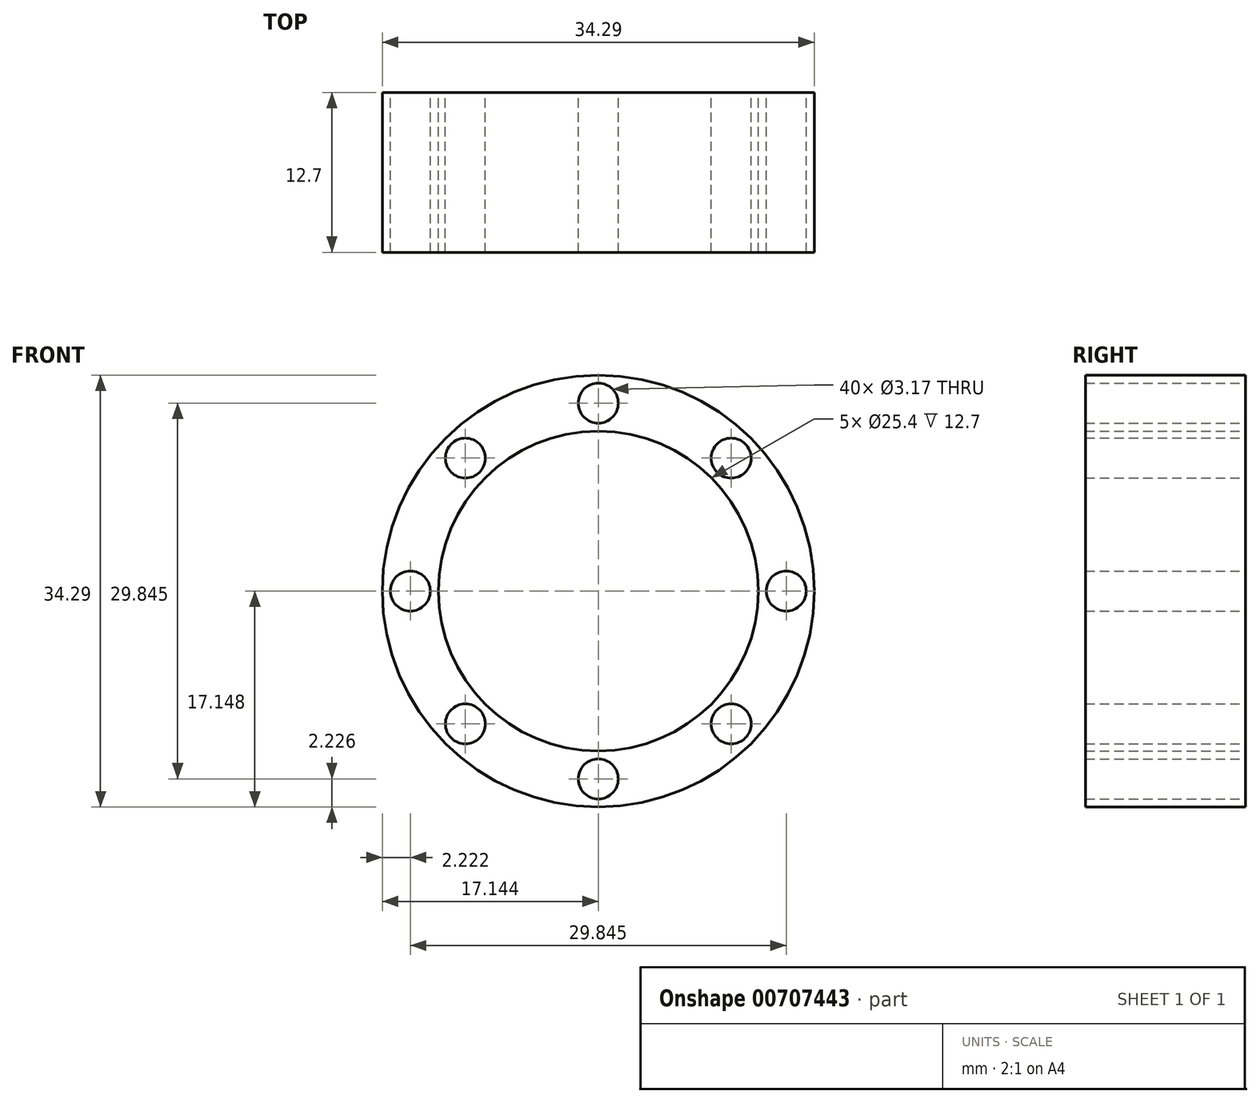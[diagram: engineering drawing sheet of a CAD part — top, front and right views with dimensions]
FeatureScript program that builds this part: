
annotation { "Feature Type Name" : "Feature", "Feature Type Description" : "" }
export const myFeature = defineFeature(function(context is Context, id is Id, definition is map)
    precondition{}
    {
        {
            var Q0;
            Q0=qCreatedBy(makeId("Front.planeOp"),FACE);
            var sketch = newSketch(context, id + "F0", { "sketchPlane" : qUnion([Q0])});
            skCircle(sketch, "E0", {"center": v(-36.52, 25.49) * mm, "radius": 17.15 * mm});
            skCircle(sketch, "E1", {"center": v(-36.52, 40.41) * mm, "radius": 1.59 * mm});
            skCircle(sketch, "E2.1.0", {"center": v(-47.07, 36.04) * mm, "radius": 1.59 * mm});
            skCircle(sketch, "E2.2.0", {"center": v(-51.44, 25.49) * mm, "radius": 1.59 * mm});
            skCircle(sketch, "E2.3.0", {"center": v(-47.07, 14.94) * mm, "radius": 1.59 * mm});
            skCircle(sketch, "E2.4.0", {"center": v(-36.52, 10.57) * mm, "radius": 1.59 * mm});
            skCircle(sketch, "E2.5.0", {"center": v(-25.96, 14.94) * mm, "radius": 1.59 * mm});
            skCircle(sketch, "E2.6.0", {"center": v(-21.6, 25.49) * mm, "radius": 1.59 * mm});
            skCircle(sketch, "E2.7.0", {"center": v(-25.96, 36.04) * mm, "radius": 1.59 * mm});
            skCircle(sketch, "E3", {"center": v(-36.52, 25.49) * mm, "radius": 12.7 * mm});
            skSolve(sketch);
        }
        {
            var Q0;
            Q0=makeQuery(id+"F0.imprint","IMPRINT",FACE,{"disambiguationData":[TD([[makeQuery(id+"F0.imprint","IMPRINT",EDGE,{"derivedFrom":sQuery(id+"F0.wireOp",EDGE,"E0")}),1.0]])]});
            extrude(context, id + "F1", {"entities" : qUnion([Q0]), "depth" : 12.7 * mm, "offsetDistance" : 25.4 * mm});
        }
    });
